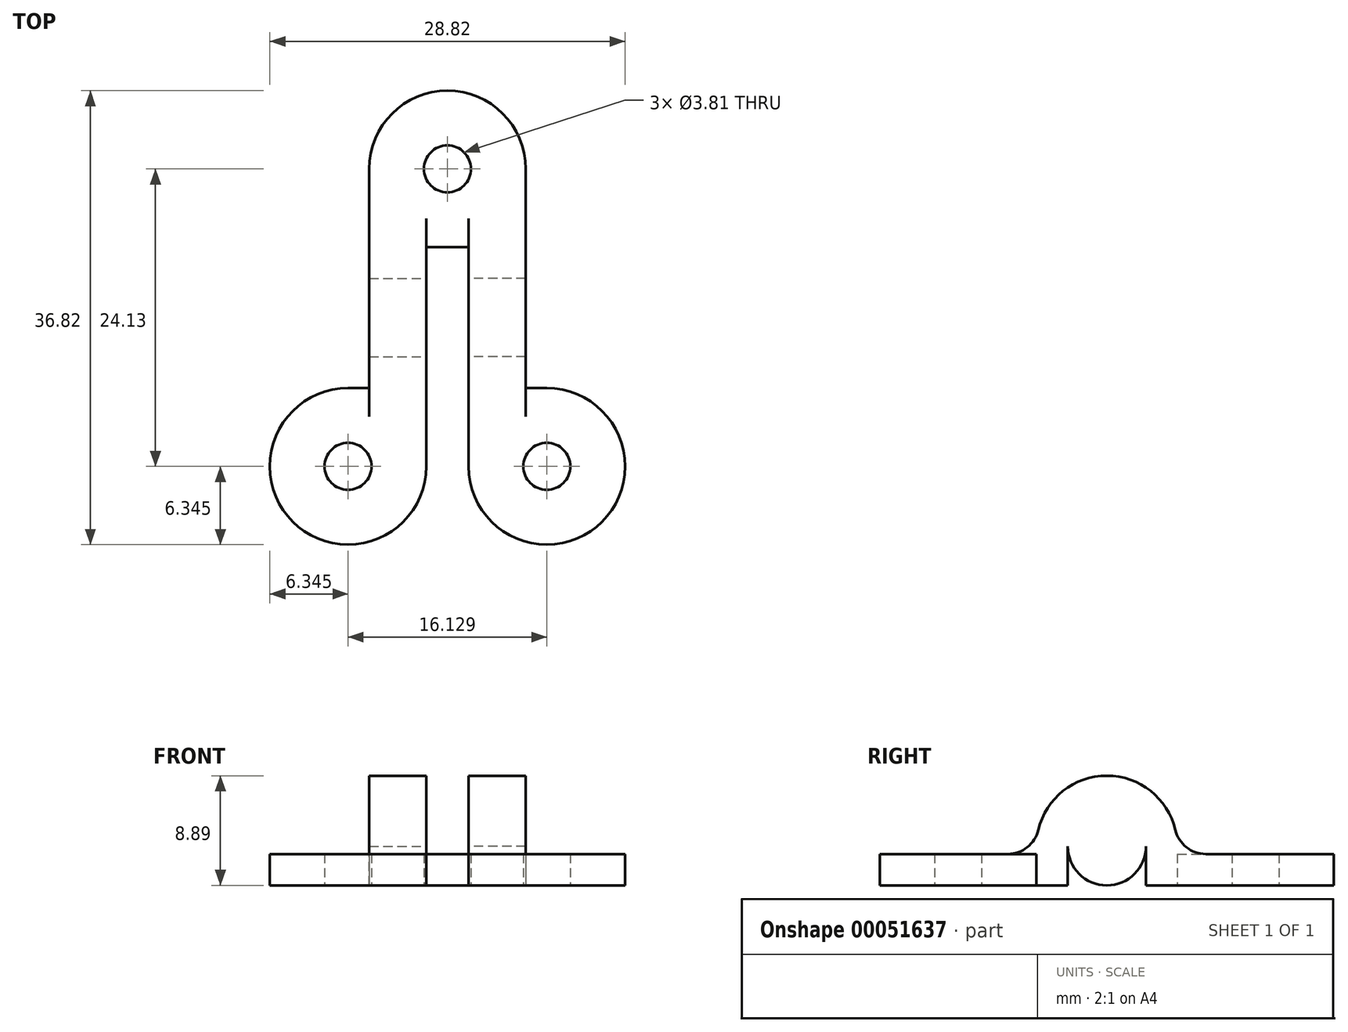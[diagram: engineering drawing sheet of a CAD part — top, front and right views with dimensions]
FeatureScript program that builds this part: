
annotation { "Feature Type Name" : "Feature", "Feature Type Description" : "" }
export const myFeature = defineFeature(function(context is Context, id is Id, definition is map)
    precondition{}
    {
        {
            var Q0;
            Q0=qCreatedBy(makeId("Right.planeOp"),FACE);
            var sketch = newSketch(context, id + "F0", { "sketchPlane" : qUnion([Q0])});
            skCircle(sketch, "E0", {"center": v(0, 3.18) * mm, "radius": 3.18 * mm});
            skSolve(sketch);
        }
        {
            var Q0;
            Q0 = qSketchRegion(id + "F0", true);
            extrude(context, id + "F1", {"entities" : qUnion([Q0]), "depth" : 6.35 * mm});
        }
        {
            var Q0;
            Q0=qCreatedBy(makeId("Right.planeOp"),FACE);
            var sketch = newSketch(context, id + "F2", { "sketchPlane" : qUnion([Q0])});
            skLineSegment(sketch, "E1", {"start": v(0, 0) * mm, "end": v(-34.92, 0) * mm});
            skLineSegment(sketch, "E2", {"start": v(3.18, 3.18) * mm, "end": v(3.18, 19.05) * mm});
            skFitSpline(sketch, "E3", {"points": [v(3.17, 19.05) * mm, v(-34.93, 0) * mm], "startDerivative": vector(-47.94, 0) * mm, "endDerivative": vector(0, -44.03) * mm});
            skPoint(sketch, "E4.orphan", {"position": v(0, 0) * mm});
            skArc(sketch, "E5.0", {"start": v(0, 0) * mm, "mid": v(2.25, 0.93) * mm, "end": v(3.18, 3.18) * mm});
            skPoint(sketch, "E6.orphan", {"position": v(3.18, 0) * mm});
            skSolve(sketch);
        }
        {
            var Q0;
            Q0=makeQuery(id+"F2.imprint","IMPRINT",FACE,{"disambiguationData":[TD([[makeQuery(id+"F2.imprint","IMPRINT",EDGE,{"derivedFrom":sQuery(id+"F2.wireOp",EDGE,"E1")}),-1.0]])]});
            extrude(context, id + "F3", {"entities" : qUnion([Q0]), "operationType" : NewBodyOperationType.ADD, "depth" : 1.71 * mm});
        }
        {
            var Q0;
            Q0=makeQuery(id+"F3.opExtrude","SWEPT_EDGE",EDGE,{"disambiguationData":[OSD([sQuery(id+"F2.wireOp",EDGE,"E2"),sQuery(id+"F2.wireOp",EDGE,"E3")])]});
            var Q1;
            Q1=makeQuery(id+"F3.opExtrude","SWEPT_EDGE",EDGE,{"disambiguationData":[OSD([sQuery(id+"F2.wireOp",EDGE,"E1"),sQuery(id+"F2.wireOp",EDGE,"E3")])]});
            fillet(context, id + "F4", {"entities" : qUnion([Q0, Q1]), "radius" : 2.54 * mm, "tangentPropagation" : true, "allowEdgeOverflow" : false});
        }
        {
            var Q0;
            Q0=qCreatedBy(makeId("Right.planeOp"),FACE);
            var sketch = newSketch(context, id + "F5", { "sketchPlane" : qUnion([Q0])});
            skArc(sketch, "E7.0", {"start": v(3.18, 3.18) * mm, "mid": v(0, 6.35) * mm, "end": v(-3.18, 3.18) * mm});
            skLineSegment(sketch, "E8", {"start": v(-3.18, 3.18) * mm, "end": v(-3.18, 0) * mm});
            skLineSegment(sketch, "E9", {"start": v(-3.18, 0) * mm, "end": v(-25.4, 0) * mm});
            skLineSegment(sketch, "E10", {"start": v(-25.4, 0) * mm, "end": v(-25.4, 2.54) * mm});
            skLineSegment(sketch, "E11", {"start": v(-25.4, 2.54) * mm, "end": v(-5.72, 2.54) * mm});
            skLineSegment(sketch, "E12", {"start": v(-5.71, 2.54) * mm, "end": v(-5.71, 3.18) * mm});
            skLineSegment(sketch, "E13", {"start": v(5.72, 3.18) * mm, "end": v(5.72, 2.54) * mm});
            skLineSegment(sketch, "E14", {"start": v(5.72, 2.54) * mm, "end": v(25.4, 2.54) * mm});
            skLineSegment(sketch, "E15", {"start": v(25.4, 2.54) * mm, "end": v(25.4, 0) * mm});
            skLineSegment(sketch, "E16", {"start": v(25.4, 0) * mm, "end": v(3.18, 0) * mm});
            skLineSegment(sketch, "E17", {"start": v(3.18, 0) * mm, "end": v(3.18, 3.18) * mm});
            skArc(sketch, "E18", {"start": v(-5.72, 3.18) * mm, "mid": v(0, 8.9) * mm, "end": v(5.72, 3.18) * mm});
            skSolve(sketch);
        }
        {
            var Q0;
            Q0 = qSketchRegion(id + "F5", true);
            extrude(context, id + "F6", {"entities" : qUnion([Q0]), "depth" : 25.82 * mm});
        }
        {
            var Q0;
            Q0=qCreatedBy(makeId("Top.planeOp"),FACE);
            var sketch = newSketch(context, id + "F7", { "sketchPlane" : qUnion([Q0])});
            skArc(sketch, "E19", {"start": v(1.71, -12.07) * mm, "mid": v(12.55, -16.56) * mm, "end": v(8.06, -5.72) * mm});
            skArc(sketch, "E20", {"start": v(6.35, 12.06) * mm, "mid": v(4.5, 16.56) * mm, "end": v(0, 18.42) * mm});
            skLineSegment(sketch, "E21", {"start": v(0, 5.71) * mm, "end": v(1.71, 5.71) * mm});
            skLineSegment(sketch, "E22", {"start": v(1.71, 5.72) * mm, "end": v(1.71, -12.07) * mm});
            skLineSegment(sketch, "E23", {"start": v(6.35, 12.06) * mm, "end": v(6.35, -5.71) * mm});
            skLineSegment(sketch, "E24", {"start": v(6.35, -5.71) * mm, "end": v(8.06, -5.71) * mm});
            skLineSegment(sketch, "E25", {"start": v(0, 5.71) * mm, "end": v(0, 10.16) * mm});
            skCircle(sketch, "E26", {"center": v(8.06, -12.07) * mm, "radius": 1.9 * mm});
            skArc(sketch, "E27", {"start": v(0, 10.16) * mm, "mid": v(1.9, 12.07) * mm, "end": v(0, 13.97) * mm});
            skLineSegment(sketch, "E28.trimOffspring", {"start": v(0, 13.97) * mm, "end": v(0, 18.42) * mm});
            skSolve(sketch);
        }
        {
            var Q0;
            Q0 = qSketchRegion(id + "F7", true);
            extrude(context, id + "F8", {"entities" : qUnion([Q0]), "operationType" : NewBodyOperationType.INTERSECT, "endBound" : BoundingType.THROUGH_ALL, "depth" : 25.4 * mm});
        }
        {
            var Q0;
            {var subQ0=sQuery(id+"F5.wireOp",EDGE,"E12");var subQ1=sQuery(id+"F5.wireOp",EDGE,"E11");Q0=makeQuery(id+"F8.boolean.opBoolean","SPLIT",EDGE,{"disambiguationData":[TD([makeQuery(id+"F8.boolean.toolComplement.opBoolean","COPY",FACE,{"derivedFrom":makeQuery(id+"F8.opExtrude","SWEPT_FACE",FACE,{"disambiguationData":[OSD([sQuery(id+"F7.wireOp",EDGE,"E22")])]})})])],"derivedFrom":makeQuery(id+"F6.opExtrude","SWEPT_EDGE",EDGE,{"disambiguationData":[OSD([subQ1,subQ0])]})});}
            var Q1;
            {var subQ0=sQuery(id+"F5.wireOp",EDGE,"E14");var subQ1=sQuery(id+"F5.wireOp",EDGE,"E13");Q1=makeQuery(id+"F8.boolean.opBoolean","SPLIT",EDGE,{"disambiguationData":[TD([makeQuery(id+"F8.boolean.toolComplement.opBoolean","COPY",FACE,{"derivedFrom":makeQuery(id+"F8.opExtrude","SWEPT_FACE",FACE,{"disambiguationData":[OSD([sQuery(id+"F7.wireOp",EDGE,"E23")])]})})])],"derivedFrom":makeQuery(id+"F6.opExtrude","SWEPT_EDGE",EDGE,{"disambiguationData":[OSD([subQ1,subQ0])]})});}
            fillet(context, id + "F9", {"entities" : qUnion([Q0, Q1]), "radius" : 2.54 * mm, "tangentPropagation" : true, "allowEdgeOverflow" : false});
        }
        {
            var Q0;
            Q0=makeQuery(id+"F1.opExtrude","SWEPT_BODY",BODY,{"disambiguationData":[OSD([sQuery(id+"F0.wireOp",EDGE,"E0")])]});
            var Q1;
            Q1=qCreatedBy(makeId("Right.planeOp"),FACE);
            mirror(context, id + "F10", {"operationType" : NewBodyOperationType.ADD, "entities" : qUnion([Q0]), "mirrorPlane" : qUnion([Q1])});
        }
        {
            var Q0;
            Q0=makeQuery(id+"F6.opExtrude","SWEPT_BODY",BODY,{"disambiguationData":[OSD([sQuery(id+"F5.wireOp",EDGE,"E7.0"),sQuery(id+"F5.wireOp",EDGE,"E8"),sQuery(id+"F5.wireOp",EDGE,"E9"),sQuery(id+"F5.wireOp",EDGE,"E10"),sQuery(id+"F5.wireOp",EDGE,"E11"),sQuery(id+"F5.wireOp",EDGE,"E12"),sQuery(id+"F5.wireOp",EDGE,"E13"),sQuery(id+"F5.wireOp",EDGE,"E14"),sQuery(id+"F5.wireOp",EDGE,"E15"),sQuery(id+"F5.wireOp",EDGE,"E16"),sQuery(id+"F5.wireOp",EDGE,"E17"),sQuery(id+"F5.wireOp",EDGE,"E18")])]});
            var Q1;
            Q1=qCreatedBy(makeId("Right.planeOp"),FACE);
            mirror(context, id + "F11", {"operationType" : NewBodyOperationType.ADD, "entities" : qUnion([Q0]), "mirrorPlane" : qUnion([Q1])});
        }
    });
